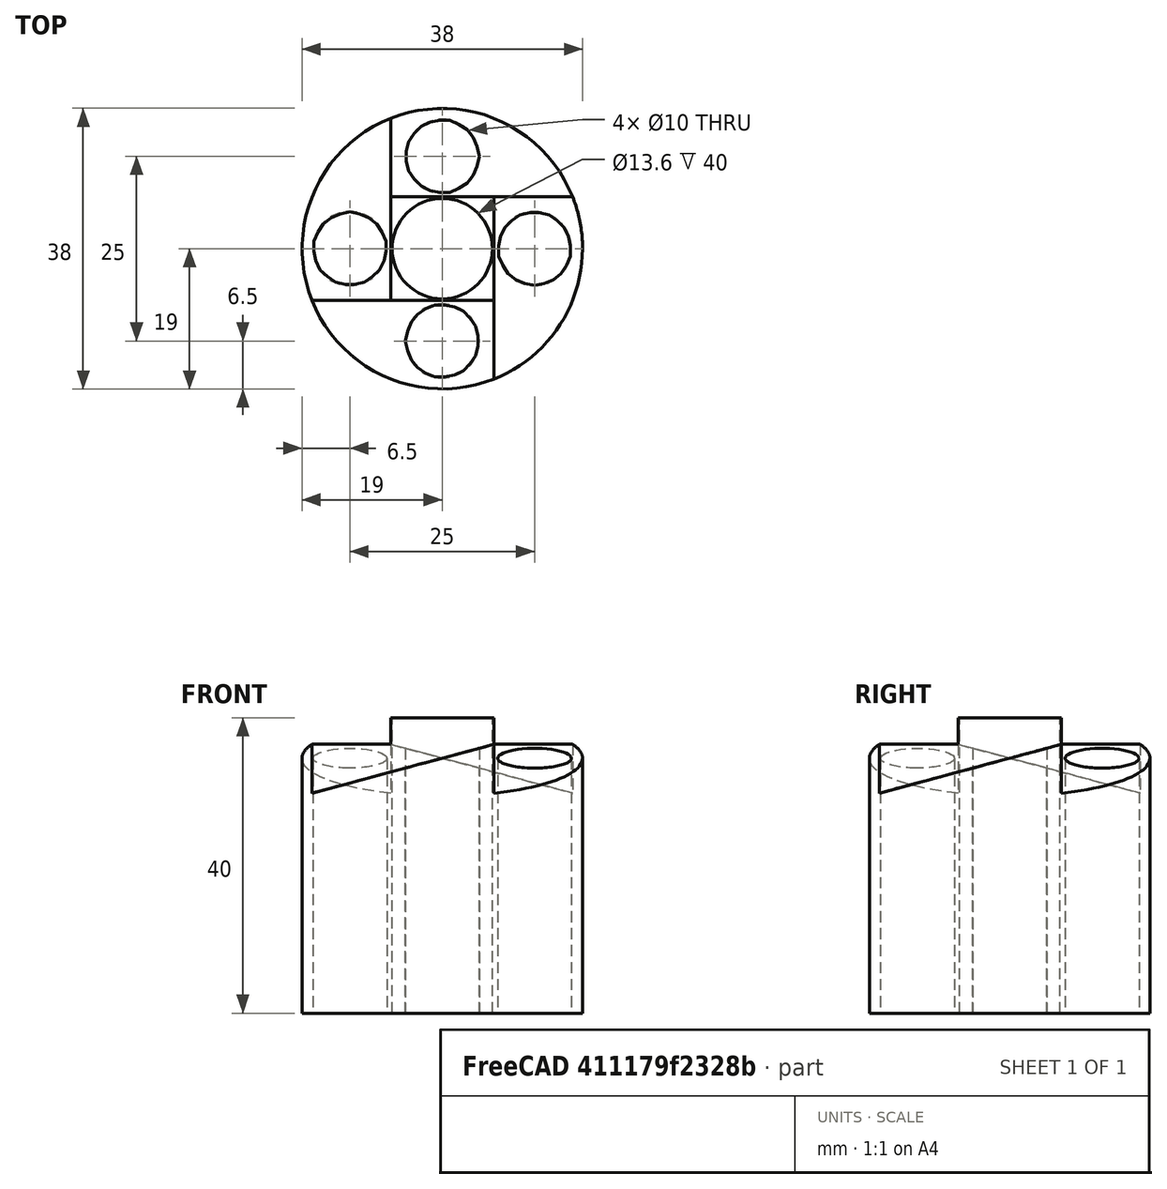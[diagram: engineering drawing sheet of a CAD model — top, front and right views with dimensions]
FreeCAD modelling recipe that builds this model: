
FCSTD DOCUMENT  (FreeCAD 0.18R4 (GitTag))
Label: cylinderFour2
License: All rights reserved
LicenseURL: http://en.wikipedia.org/wiki/All_rights_reserved
objects: Part::Cylinder×11, Part::MultiFuse×11, Part::Box×4, Part::Cut×3, Part::Feature×1
note: 30 computed .brp shape members not serialized (recipe doc carries the construction recipe); baked Part::Feature solids carry a one-line shape summary decoded from their .brp

FEATURE [Part::Cylinder] Cylinder
  Angle = 360
  AttacherType = Attacher::AttachEngine3D
  Height = 40
  Radius = 19
FEATURE [Part::Cylinder] Cylinder001
  Angle = 360
  AttacherType = Attacher::AttachEngine3D
  Height = 50
  Placement = pos=(0,12.5,0) rot=(0,0,1;0rad)
  Radius = 5
FEATURE [Part::Cylinder] Cylinder003  label="bevilPin"
  Angle = 360
  AttacherType = Attacher::AttachEngine3D
  Height = 50
  Radius = 6.35
FEATURE [Part::Cylinder] Cylinder004  label="bevilPin001"
  Angle = 360
  AttacherType = Attacher::AttachEngine3D
  Height = 50
  Radius = 6.35
FEATURE [Part::Box] Box  label="Cube"
  AttacherType = Attacher::AttachEngine3D
  Height = 30
  Length = 40
  Placement = pos=(-19.5582,7,39.7598) rot=(0,1,0;0.261799rad)
  Width = 20
FEATURE [Part::MultiFuse] Fusion
  Shapes = -> [Cylinder001,Box]
FEATURE [Part::MultiFuse] Fusion001
  Shapes = -> [Fusion,Cylinder004]
FEATURE [Part::Box] Box001  label="Cube001"
  AttacherType = Attacher::AttachEngine3D
  Height = 30
  Length = 40
  Placement = pos=(-19.5582,7,39.7598) rot=(0,1,0;0.261799rad)
  Width = 20
FEATURE [Part::Cylinder] Cylinder005
  Angle = 360
  AttacherType = Attacher::AttachEngine3D
  Height = 50
  Placement = pos=(0,12.5,0) rot=(0,0,1;0rad)
  Radius = 5
FEATURE [Part::Cylinder] Cylinder006  label="bevilPin002"
  Angle = 360
  AttacherType = Attacher::AttachEngine3D
  Height = 50
  Radius = 6.35
FEATURE [Part::MultiFuse] Fusion002
  Shapes = -> [Cylinder005,Box001]
FEATURE [Part::MultiFuse] Fusion003
  Placement = pos=(0,0,0) rot=(0,0,1;3.14159rad)
  Shapes = -> [Fusion002,Cylinder006]
FEATURE [Part::MultiFuse] Fusion004
  Shapes = -> [Fusion003,Fusion001]
FEATURE [Part::Box] Box002  label="Cube002"
  AttacherType = Attacher::AttachEngine3D
  Height = 30
  Length = 40
  Placement = pos=(-19.5582,7,39.7598) rot=(0,1,0;0.261799rad)
  Width = 20
FEATURE [Part::Box] Box003  label="Cube003"
  AttacherType = Attacher::AttachEngine3D
  Height = 30
  Length = 40
  Placement = pos=(-19.5582,7,39.7598) rot=(0,1,0;0.261799rad)
  Width = 20
FEATURE [Part::Cylinder] Cylinder007
  Angle = 360
  AttacherType = Attacher::AttachEngine3D
  Height = 50
  Placement = pos=(0,12.5,0) rot=(0,0,1;0rad)
  Radius = 5
FEATURE [Part::Cylinder] Cylinder008  label="bevilPin003"
  Angle = 360
  AttacherType = Attacher::AttachEngine3D
  Height = 50
  Radius = 6.35
FEATURE [Part::Cylinder] Cylinder009
  Angle = 360
  AttacherType = Attacher::AttachEngine3D
  Height = 50
  Placement = pos=(0,12.5,0) rot=(0,0,1;0rad)
  Radius = 5
FEATURE [Part::Cylinder] Cylinder010  label="bevilPin004"
  Angle = 360
  AttacherType = Attacher::AttachEngine3D
  Height = 50
  Radius = 6.35
FEATURE [Part::MultiFuse] Fusion005
  Shapes = -> [Cylinder007,Box002]
FEATURE [Part::MultiFuse] Fusion006
  Shapes = -> [Fusion005,Cylinder008]
FEATURE [Part::MultiFuse] Fusion007
  Shapes = -> [Cylinder009,Box003]
FEATURE [Part::MultiFuse] Fusion008
  Placement = pos=(0,0,0) rot=(0,0,1;3.14159rad)
  Shapes = -> [Fusion007,Cylinder010]
FEATURE [Part::MultiFuse] Fusion009
  Placement = pos=(0,0,0) rot=(0,0,-1;1.5708rad)
  Shapes = -> [Fusion008,Fusion006]
FEATURE [Part::MultiFuse] Fusion010
  Shapes = -> [Fusion009,Fusion004]
FEATURE [Part::Cut] Cut
  Base = -> Cylinder
  Tool = -> Fusion010
FEATURE [Part::Cut] Cut001
  Base = -> Cut
  Tool = -> Cylinder003
FEATURE [Part::Cylinder] Cylinder011  label="Cylinder010"
  Angle = 360
  AttacherType = Attacher::AttachEngine3D
  Height = 60
  Radius = 6.8
FEATURE [Part::Cut] Cut002
  Base = -> Cut001
  Tool = -> Cylinder011
FEATURE [Part::Feature] Cut002_solid  label="Cut002 (Solid)"
  shape: bbox 38 x 38 x 40 mm, 16 faces (baked)
